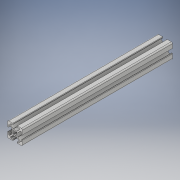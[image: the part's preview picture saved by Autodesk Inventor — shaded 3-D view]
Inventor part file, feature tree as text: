
AUTODESK INVENTOR PART (.ipt)
format: ipt  version: 2025 (Build 290162000, 162)  size: 239,616 bytes
history: native  units: mm
features: extrude x1, sketch x1
ambient origin geometry x8: Origin, YZ Plane, XZ Plane, XY Plane, X Axis, Y Axis, Z Axis, Center Point
bodies: Solid1 (feature_tree)
feature tree (2):
  extrude  "Extrusion1"  [1 undecoded]
  sketch  "Sketch_1"  dims[d0=200.0mm d1=0.0mm]
note: 1 required parameter value undecoded (feature->parameter linkage not recoverable at this tier; creation-order binding heuristic only, values carry confidence <= 0.55)
